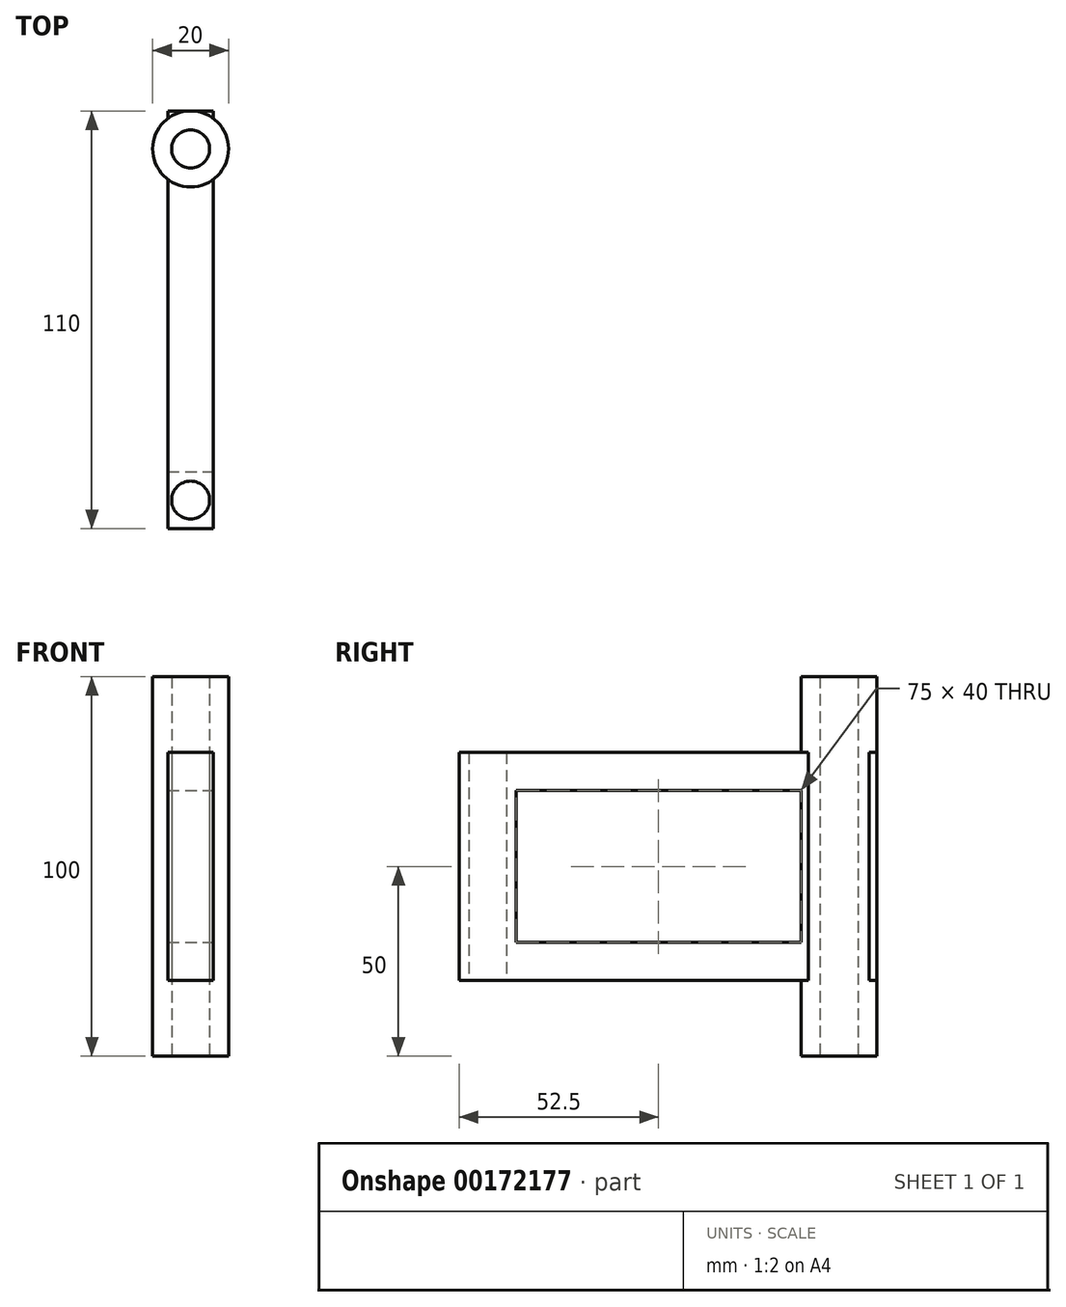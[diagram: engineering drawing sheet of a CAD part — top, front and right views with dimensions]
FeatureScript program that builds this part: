
annotation { "Feature Type Name" : "Feature", "Feature Type Description" : "" }
export const myFeature = defineFeature(function(context is Context, id is Id, definition is map)
    precondition{}
    {
        {
            var Q0;
            Q0=qCreatedBy(makeId("Top.planeOp"),FACE);
            var sketch = newSketch(context, id + "F0", { "sketchPlane" : qUnion([Q0])});
            skCircle(sketch, "E0", {"center": v(0, 0) * mm, "radius": 10 * mm});
            skSolve(sketch);
        }
        {
            var Q0;
            Q0 = qSketchRegion(id + "F0", true);
            extrude(context, id + "F1", {"entities" : qUnion([Q0]), "depth" : 100 * mm});
        }
        {
            var Q0;
            Q0=qCreatedBy(makeId("Front.planeOp"),FACE);
            var sketch = newSketch(context, id + "F2", { "sketchPlane" : qUnion([Q0])});
            skLineSegment(sketch, "E1.bottom", {"start": v(6, 20) * mm, "end": v(-6, 20) * mm});
            skLineSegment(sketch, "E1.top", {"start": v(6, 80) * mm, "end": v(-6, 80) * mm});
            skLineSegment(sketch, "E1.left", {"start": v(6, 20) * mm, "end": v(6, 80) * mm});
            skLineSegment(sketch, "E1.right", {"start": v(-6, 20) * mm, "end": v(-6, 80) * mm});
            skPoint(sketch, "E1.middle", {"position": v(0, 50) * mm});
            skSolve(sketch);
        }
        {
            var Q0;
            Q0 = qSketchRegion(id + "F2", true);
            extrude(context, id + "F3", {"entities" : qUnion([Q0]), "operationType" : NewBodyOperationType.ADD, "depth" : 100 * mm, "hasSecondDirection" : true, "secondDirectionOppositeDirection" : true, "secondDirectionDepth" : 10 * mm});
        }
        {
            var Q0;
            Q0=makeQuery(id+"F3.opExtrude","SWEPT_FACE",FACE,{"disambiguationData":[OSD([sQuery(id+"F2.wireOp",EDGE,"E1.left")])]});
            var sketch = newSketch(context, id + "F4", { "sketchPlane" : qUnion([Q0])});
            skLineSegment(sketch, "E2.bottom", {"start": v(-10, 30) * mm, "end": v(-85, 30) * mm});
            skLineSegment(sketch, "E2.top", {"start": v(-10, 70) * mm, "end": v(-85, 70) * mm});
            skLineSegment(sketch, "E2.left", {"start": v(-10, 30) * mm, "end": v(-10, 70) * mm});
            skLineSegment(sketch, "E2.right", {"start": v(-85, 30) * mm, "end": v(-85, 70) * mm});
            skSolve(sketch);
        }
        {
            var Q0;
            Q0 = qSketchRegion(id + "F4", true);
            extrude(context, id + "F5", {"entities" : qUnion([Q0]), "operationType" : NewBodyOperationType.REMOVE, "endBound" : BoundingType.UP_TO_NEXT, "oppositeDirection" : true, "depth" : 25 * mm});
        }
        {
            var Q0;
            Q0=qCreatedBy(makeId("Top.planeOp"),FACE);
            var sketch = newSketch(context, id + "F6", { "sketchPlane" : qUnion([Q0])});
            skCircle(sketch, "E3", {"center": v(0, 0) * mm, "radius": 5 * mm});
            skSolve(sketch);
        }
        {
            var Q0;
            Q0 = qSketchRegion(id + "F6", true);
            extrude(context, id + "F7", {"entities" : qUnion([Q0]), "operationType" : NewBodyOperationType.REMOVE, "endBound" : BoundingType.UP_TO_NEXT, "depth" : 25 * mm});
        }
        {
            var Q0;
            {var subQ0=sQuery(id+"F2.wireOp",EDGE,"E1.left");var subQ1=sQuery(id+"F2.wireOp",EDGE,"E1.right");var subQ2=sQuery(id+"F2.wireOp",EDGE,"E1.bottom");var subQ3=makeQuery(id+"F3.opExtrude","SWEPT_FACE",FACE,{"disambiguationData":[OSD([subQ2])]});Q0=makeQuery(id+"F3.boolean.opBoolean","SPLIT",FACE,{"disambiguationData":[TD([makeQuery(id+"F1.opExtrude","SWEPT_FACE",FACE,{"disambiguationData":[OSD([sQuery(id+"F0.wireOp",EDGE,"E0")])]}),subQ3,makeQuery(id+"F3.opExtrude","CAP_FACE",FACE,{"disambiguationData":[OSD([subQ2,sQuery(id+"F2.wireOp",EDGE,"E1.top"),subQ0,subQ1])],"isStart":false}),makeQuery(id+"F3.opExtrude","SWEPT_FACE",FACE,{"disambiguationData":[OSD([subQ0])]}),makeQuery(id+"F3.opExtrude","SWEPT_FACE",FACE,{"disambiguationData":[OSD([subQ1])]})])],"derivedFrom":subQ3});}
            var sketch = newSketch(context, id + "F8", { "sketchPlane" : qUnion([Q0])});
            skCircle(sketch, "E4", {"center": v(0, 92.5) * mm, "radius": 5 * mm});
            skPoint(sketch, "E5", {"position": v(0, 10) * mm});
            skSolve(sketch);
        }
        {
            var Q0;
            Q0 = qSketchRegion(id + "F8", true);
            extrude(context, id + "F9", {"entities" : qUnion([Q0]), "operationType" : NewBodyOperationType.REMOVE, "endBound" : BoundingType.THROUGH_ALL, "oppositeDirection" : true, "depth" : 25 * mm});
        }
    });
